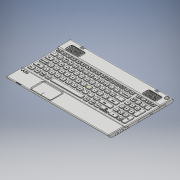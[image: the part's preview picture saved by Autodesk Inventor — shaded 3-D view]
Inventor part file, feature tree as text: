
AUTODESK INVENTOR PART (.ipt)
format: ipt  version: 2017 (Build 210142000, 142)  size: 9,598,464 bytes
history: native  units: mm
features: sketch x58, extrude x57, fillet x46, pattern_linear x11, projected_geometry x10, mirror x3, plane x2, hole x1
ambient origin geometry x8: Origin, YZ Plane, XZ Plane, XY Plane, X Axis, Y Axis, Z Axis, Center Point
bodies: Solid1 (feature_tree), Solid2 (feature_tree), Solid3 (feature_tree)
feature tree (188):
  extrude  "Extrusion1"  Depth=250.0mm
  extrude  "Extrusion2"  Depth=22.0mm
  mirror  "Mirror1"
  extrude  "Extrusion3"  Depth=45.0mm
  extrude  "Extrusion4"  Depth=3.0mm
  extrude  "Extrusion5"  Depth=43.75mm TaperAngle=0.0deg
  extrude  "Extrusion6"  Depth=408.75mm TaperAngle=0.0deg
  fillet  "Fillet1"  Radius=5.0mm
  fillet  "Fillet2"  Radius=5.0mm
  extrude  "Extrusion7"  Depth=3.0mm TaperAngle=0.0deg
  extrude  "Extrusion8"  Depth=1.0mm
  fillet  "Fillet3"  [1 undecoded]
  fillet  "Fillet4"  Radius=340.0mm
  plane  "Work Plane1"
  extrude  "Extrusion9"  Depth=0.5mm
  pattern_linear  "Rectangular Pattern1"  Count1=34 Spacing1=0.0mm
  sketch  "Sketch10"  dims[d41=340.0mm d42=0.0mm d43=340.0mm d44=0.0mm d45=30.0mm d47=16.5mm]
  fillet  "Fillet5"  Radius=160.0mm
  extrude  "Extrusion10"  Depth=340.0mm TaperAngle=0.0deg
  pattern_linear  "Rectangular Pattern2"  Count1=3 Spacing1=16.5mm
  extrude  "Extrusion11"  Depth=140.0mm
  extrude  "Extrusion12"  Depth=7.63472mm TaperAngle=0.0deg
  pattern_linear  "Rectangular Pattern3"  Count1=13 Spacing1=18.0mm
  extrude  "Extrusion13"  Depth=120.0mm
  pattern_linear  "Rectangular Pattern4"  Count1=11 Spacing1=19.5mm
  extrude  "Extrusion14"  Depth=130.0mm
  extrude  "Extrusion15"  Depth=5.0mm
  extrude  "Extrusion16"  Depth=580.61528mm TaperAngle=0.0deg
  extrude  "Extrusion17"  Depth=20.0mm
  extrude  "Extrusion18"  Depth=2.0mm
  pattern_linear  "Rectangular Pattern5"  Count1=15 Spacing1=4.0mm
  sketch  "Sketch19"  dims[d80=7.63472mm d81=0.0mm d82=130.0mm d84=19.0mm]
  extrude  "Extrusion19"  Depth=4.0mm TaperAngle=0.0deg
  pattern_linear  "Rectangular Pattern6"  Count1=15 Spacing1=6.0mm
  extrude  "Extrusion20"  Depth=0.5mm
  pattern_linear  "Rectangular Pattern7"  Count1=4  [1 undecoded]
  extrude  "Extrusion21"  Depth=0.1mm
  pattern_linear  "Rectangular Pattern8"  Count1=7 Spacing1=3.2mm
  extrude  "Extrusion22"  Depth=10.0mm TaperAngle=0.0deg
  fillet  "Fillet6"  Radius=10.0mm
  fillet  "Fillet7"  Radius=1.0mm
  extrude  "Extrusion23"  Depth=14.5mm TaperAngle=0.0deg
  extrude  "Extrusion24"  Depth=0.5mm
  mirror  "Mirror2"
  fillet  "Fillet8"  Radius=0.5mm
  fillet  "Fillet9"  Radius=1.0mm
  fillet  "Fillet10"  Radius=1.0mm
  extrude  "Extrusion25"  Depth=0.5mm
  pattern_linear  "Rectangular Pattern9"  Spacing1=1.0mm  [1 undecoded]
  sketch  "Sketch27"  dims[d107=0.1mm]
  extrude  "Extrusion26"  Depth=0.5mm
  extrude  "Extrusion27"  Depth=0.5mm
  extrude  "Extrusion28"  Depth=0.5mm
  fillet  "Fillet11"  Radius=1.0mm
  extrude  "Extrusion29"  Depth=0.5mm
  extrude  "Extrusion30"  Depth=0.5mm
  extrude  "Extrusion31"  Depth=0.5mm
  extrude  "Extrusion32"  Depth=0.5mm
  extrude  "Extrusion33"  Depth=0.5mm
  fillet  "Fillet12"  Radius=1.0mm
  extrude  "Extrusion34"  Depth=0.5mm
  extrude  "Extrusion35"  Depth=0.5mm
  extrude  "Extrusion36"  Depth=0.5mm
  extrude  "Extrusion37"  Depth=0.5mm
  fillet  "Fillet13"  Radius=1.0mm
  fillet  "Fillet14"  Radius=1.0mm
  extrude  "Extrusion38"  Depth=0.5mm TaperAngle=0.0deg
  extrude  "Extrusion39"  Depth=0.5mm TaperAngle=0.0deg
  fillet  "Fillet15"  Radius=39.5mm
  fillet  "Fillet16"  Radius=2.0mm
  extrude  "Extrusion40"  Depth=0.5mm
  fillet  "Fillet17"  Radius=0.5mm
  fillet  "Fillet18"  Radius=0.1mm
  extrude  "Extrusion41"  Depth=0.1mm TaperAngle=0.0deg
  extrude  "Extrusion42"  [1 undecoded]
  pattern_linear  "Rectangular Pattern10"  Spacing1=1.4mm  [1 undecoded]
  extrude  "Extrusion43"  Depth=0.5mm
  fillet  "Fillet19"  Radius=0.5mm
  fillet  "Fillet20"  [1 undecoded]
  hole  "Hole1"  [1 undecoded]
  fillet  "Fillet21"  [1 undecoded]
  pattern_linear  "Rectangular Pattern11"  [2 undecoded]
  mirror  "Mirror3"
  extrude  "Extrusion44"  [1 undecoded]
  extrude  "Extrusion45"  [1 undecoded]
  fillet  "Fillet22"  [1 undecoded]
  extrude  "Extrusion46"  [1 undecoded]
  extrude  "Extrusion47"  [1 undecoded]
  extrude  "Extrusion48"  [1 undecoded]
  fillet  "Fillet23"  [1 undecoded]
  extrude  "Extrusion49"  [1 undecoded]
  fillet  "Fillet24"  [1 undecoded]
  fillet  "Fillet25"  [1 undecoded]
  fillet  "Fillet26"  [1 undecoded]
  fillet  "Fillet27"  [1 undecoded]
  fillet  "Fillet28"  [1 undecoded]
  fillet  "Fillet29"  [1 undecoded]
  fillet  "Fillet30"  [1 undecoded]
  fillet  "Fillet31"  [1 undecoded]
  fillet  "Fillet32"  [1 undecoded]
  fillet  "Fillet33"  [1 undecoded]
  fillet  "Fillet34"  [1 undecoded]
  fillet  "Fillet35"  [1 undecoded]
  fillet  "Fillet36"  [1 undecoded]
  fillet  "Fillet37"  [1 undecoded]
  fillet  "Fillet38"  [1 undecoded]
  fillet  "Fillet39"  [1 undecoded]
  fillet  "Fillet40"  [1 undecoded]
  fillet  "Fillet41"  [1 undecoded]
  fillet  "Fillet42"  [1 undecoded]
  fillet  "Fillet43"  [1 undecoded]
  extrude  "Extrusion50"  [1 undecoded]
  extrude  "Extrusion51"  [1 undecoded]
  extrude  "Extrusion52"  [1 undecoded]
  extrude  "Extrusion53"  [1 undecoded]
  fillet  "Fillet44"  [1 undecoded]
  sketch  "Sketch55"  dims[d156=2.0mm d157=6.0mm d158=4.0mm d159=2.0mm d160=90.0deg d161=5.0mm d162=20.594885mm d163=0.1mm d164=70.0mm d166=3.2mm]
  sketch  "Sketch56"  dims[d167=140.0mm d169=3.1mm d170=10.0mm d171=0.0mm d172=10.0mm d173=0.0mm d174=1.0mm]
  extrude  "Extrusion54"  [1 undecoded]
  extrude  "Extrusion55"  [1 undecoded]
  extrude  "Extrusion56"  [1 undecoded]
  plane  "Work Plane2"
  extrude  "Extrusion57"  [1 undecoded]
  fillet  "Fillet45"  [1 undecoded]
  fillet  "Fillet46"  [1 undecoded]
  sketch  "Sketch1"  dims[d0=360.0mm d1=250.0mm]
  sketch  "Sketch2"  dims[d2=15.0mm d3=0.0mm d5=22.0mm]
  sketch  "Sketch3"  dims[d6=11.0mm d7=45.0mm]
  sketch  "Sketch4"  dims[d8=43.75mm d9=0.0mm d10=3.0mm]
  sketch  "Sketch5"  dims[d11=33.5mm d12=280.625mm d13=0.0mm d14=0.0mm d15=43.75mm d16=0.0mm]
  sketch  "Sketch6"  dims[d17=43.75mm d18=0.0mm d19=408.75mm d20=0.0mm d21=5.0mm d22=5.0mm]
  sketch  "Sketch7"  dims[d23=412.5mm d24=0.0mm d25=3.0mm d26=0.0mm]
  sketch  "Sketch8"  dims[d27=5.0mm d28=1.0mm d29=-10.0mm d30=340.0mm d31=0.0mm]
  sketch  "Sketch9"  dims[d32=60.0mm d34=20.0mm d35=0.5mm d36=340.0mm d37=0.0mm d38=160.0mm d40=17.0mm]
  sketch  "Sketch11"  dims[d48=340.0mm d49=0.0mm d50=140.0mm d52=18.0mm]
  sketch  "Sketch12"  dims[d53=340.0mm d54=0.0mm d55=7.63472mm d56=0.0mm]
  sketch  "Sketch13"  dims[d57=3.817mm d58=0.0mm]
  sketch  "Sketch14"  dims[d59=7.63472mm d60=3.817mm d61=0.0mm d62=0.0mm]
  projected_geometry  "Projected Loop1"
  sketch  "Sketch15"  dims[d63=7.63472mm d64=0.0mm]
  projected_geometry  "Projected Loop2"
  projected_geometry  "Projected Loop3"
  sketch  "Sketch16"  dims[d65=7.63472mm d66=0.0mm d67=130.0mm d69=18.0mm]
  projected_geometry  "Projected Loop4"
  sketch  "Sketch17"  dims[d70=7.63472mm d71=0.0mm d72=120.0mm d74=19.0mm]
  projected_geometry  "Projected Loop5"
  sketch  "Sketch18"  dims[d75=7.63472mm d76=0.0mm d77=110.0mm d79=19.5mm]
  sketch  "Sketch20"  dims[d85=106.36528mm d86=0.0mm d87=5.0mm]
  sketch  "Sketch21"  dims[d88=1.0mm d89=580.61528mm d90=0.0mm]
  sketch  "Sketch22"  dims[d91=580.61528mm d92=0.0mm d93=20.0mm]
  sketch  "Sketch23"  dims[d94=2.0mm d95=2.0mm]
  projected_geometry  "Projected Loop6"
  sketch  "Sketch24"  dims[d96=5.0mm d97=0.0mm d98=150.0mm d100=4.0mm]
  sketch  "Sketch25"  dims[d101=2.0mm d102=0.0mm d103=4.0mm d104=0.0mm]
  sketch  "Sketch26"  dims[d105=1.5mm d106=0.0mm]
  sketch  "Sketch28"  dims[d108=10.0mm d109=0.0mm]
  sketch  "Sketch29"  dims[d110=4.5mm]
  sketch  "Sketch30"  dims[d111=4.5mm]
  sketch  "Sketch31"  dims[d112=5.0mm d113=0.0mm]
  sketch  "Sketch32"  dims[d114=5.0mm d115=0.0mm]
  sketch  "Sketch33"  dims[d116=2.0mm]
  sketch  "Sketch34"  dims[d117=5.0mm d118=0.0mm]
  sketch  "Sketch35"  dims[d119=5.0mm d120=0.0mm]
  sketch  "Sketch36"  dims[d121=0.1mm]
  sketch  "Sketch37"  dims[d122=10.0mm d123=0.0mm]
  sketch  "Sketch38"  dims[d125=8.5mm d126=0.0mm]
  sketch  "Sketch39"  dims[d127=8.5mm d128=0.0mm]
  sketch  "Sketch40"  dims[d129=1.0mm d130=0.0mm]
  sketch  "Sketch41"  dims[d131=1.0mm]
  sketch  "Sketch42"  dims[d132=1.0mm]
  sketch  "Sketch43"  dims[d133=10.0mm d134=0.0mm]
  sketch  "Sketch44"  dims[d135=3.0mm d136=0.0mm]
  sketch  "Sketch45"  dims[d137=2.0mm]
  sketch  "Sketch46"  dims[d138=2.0mm]
  sketch  "Sketch47"  dims[d139=1.0mm d140=0.0mm]
  sketch  "Sketch48"  dims[d141=5.0mm]
  projected_geometry  "Projected Loop7"
  sketch  "Sketch49"  dims[d142=5.0mm]
  sketch  "Sketch50"  dims[d143=1.0mm d144=0.0mm]
  sketch  "Sketch51"  dims[d145=1.0mm d146=0.0mm d147=150.0mm d149=6.0mm]
  sketch  "Sketch52"  dims[d150=0.5mm d151=0.0mm d152=5.0mm]
  projected_geometry  "Projected Loop8"
  sketch  "Sketch53"  dims[d153=1.0mm d154=40.0mm]
  projected_geometry  "Projected Loop9"
  sketch  "Sketch54"  dims[d155=20.0mm]
  projected_geometry  "Projected Loop10"
  sketch  "Sketch57"  dims[d175=93.25mm d176=0.0mm d177=14.5mm d178=0.0mm]
  sketch  "Sketch58"  dims[d179=1.0mm d180=0.0mm d181=5.0mm d182=0.5mm d183=0.0mm d184=1.0mm d185=1.0mm d186=1.0mm d187=1.0mm d188=1.0mm d189=1.0mm d190=1.0mm d191=1.0mm d192=1.0mm d193=1.0mm d194=1.0mm d195=1.0mm d196=1.0mm d197=1.0mm d198=1.0mm d199=1.0mm d200=1.0mm d201=1.0mm d202=1.0mm d203=1.0mm d204=283.25mm d205=0.0mm d206=3.75mm d207=317.75mm d208=0.0mm d209=0.0mm d210=39.5mm d211=0.0mm d212=2.0mm d213=0.0mm d214=1.0mm d215=0.5mm d216=0.0mm d217=0.1mm d218=0.0mm d219=0.1mm d220=0.0mm d221=-110.75mm d222=1.4mm d223=0.0mm d224=0.5mm d225=0.5mm]
note: 49 required parameter values undecoded (feature->parameter linkage not recoverable at this tier; creation-order binding heuristic only, values carry confidence <= 0.55)
